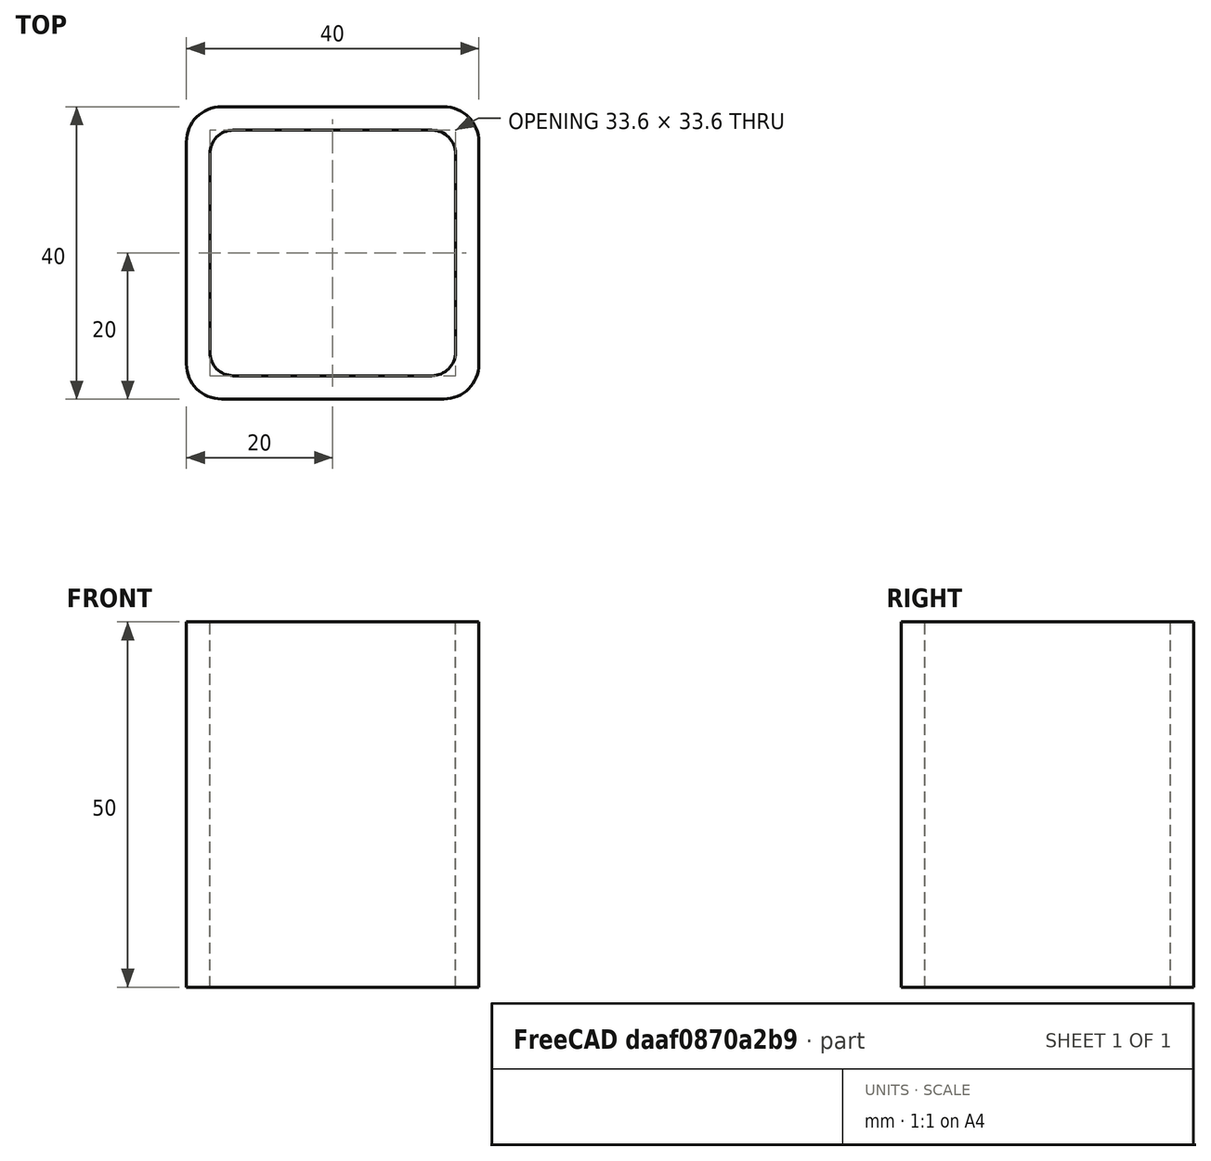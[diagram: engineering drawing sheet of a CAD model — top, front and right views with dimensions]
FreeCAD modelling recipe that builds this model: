
FCSTD DOCUMENT  (FreeCAD 0.15R4671 (Git))
Label: Square hollow section 40x40x3.2 EN10219 S235JRH
License: All rights reserved
LicenseURL: http://en.wikipedia.org/wiki/All_rights_reserved
objects: Sketcher::SketchObject×1, Part::Extrusion×1
note: 2 computed .brp shape members not serialized (recipe doc carries the construction recipe); baked Part::Feature solids carry a one-line shape summary decoded from their .brp

FEATURE [Sketcher::SketchObject] Sketch
  sketch-geometry (16):
    g0: LineSegment StartX=-13.6 StartY=16.8 StartZ=0 EndX=13.6 EndY=16.8 EndZ=0
    g1: LineSegment StartX=16.8 StartY=13.6 StartZ=0 EndX=16.8 EndY=-13.6 EndZ=0
    g2: LineSegment StartX=13.6 StartY=-16.8 StartZ=0 EndX=-13.6 EndY=-16.8 EndZ=0
    g3: LineSegment StartX=-16.8 StartY=-13.6 StartZ=0 EndX=-16.8 EndY=13.6 EndZ=0
    g4: LineSegment StartX=-15.2 StartY=20 StartZ=0 EndX=15.2 EndY=20 EndZ=0
    g5: LineSegment StartX=20 StartY=15.2 StartZ=0 EndX=20 EndY=-15.2 EndZ=0
    g6: LineSegment StartX=15.2 StartY=-20 StartZ=0 EndX=-15.2 EndY=-20 EndZ=0
    g7: LineSegment StartX=-20 StartY=-15.2 StartZ=0 EndX=-20 EndY=15.2 EndZ=0
    g8: ArcOfCircle CenterX=-13.6 CenterY=13.6 CenterZ=0 NormalX=0 NormalY=0 NormalZ=1 Radius=3.2 StartAngle=1.5708 EndAngle=3.14159
    g9: ArcOfCircle CenterX=13.6 CenterY=13.6 CenterZ=0 NormalX=0 NormalY=0 NormalZ=1 Radius=3.2 StartAngle=0 EndAngle=1.5708
    g10: ArcOfCircle CenterX=13.6 CenterY=-13.6 CenterZ=0 NormalX=0 NormalY=0 NormalZ=1 Radius=3.2 StartAngle=4.71239 EndAngle=6.28319
    g11: ArcOfCircle CenterX=-13.6 CenterY=-13.6 CenterZ=0 NormalX=0 NormalY=0 NormalZ=1 Radius=3.2 StartAngle=3.14159 EndAngle=4.71239
    g12: ArcOfCircle CenterX=15.2 CenterY=15.2 CenterZ=0 NormalX=0 NormalY=0 NormalZ=1 Radius=4.8 StartAngle=0 EndAngle=1.5708
    g13: ArcOfCircle CenterX=15.2 CenterY=-15.2 CenterZ=0 NormalX=0 NormalY=0 NormalZ=1 Radius=4.8 StartAngle=4.71239 EndAngle=6.28319
    g14: ArcOfCircle CenterX=-15.2 CenterY=-15.2 CenterZ=0 NormalX=0 NormalY=0 NormalZ=1 Radius=4.8 StartAngle=3.14159 EndAngle=4.71239
    g15: ArcOfCircle CenterX=-15.2 CenterY=15.2 CenterZ=0 NormalX=0 NormalY=0 NormalZ=1 Radius=4.8 StartAngle=1.5708 EndAngle=3.14159
  constraints (36):
    c: Horizontal(g2)
    c: Vertical(g3)
    c: Horizontal(g6)
    c: Vertical(g7)
    c: Tangent(g3,g8) = 1.5708
    c: Tangent(g0,g8) = 1.5708
    c: Tangent(g0,g9) = 1.5708
    c: Tangent(g1,g9) = 1.5708
    c: Tangent(g1,g10) = 1.5708
    c: Tangent(g2,g10) = 1.5708
    c: Tangent(g2,g11) = 1.5708
    c: Tangent(g3,g11) = 1.5708
    c: Tangent(g4,g12) = 1.5708
    c: Tangent(g5,g12) = 1.5708
    c: Tangent(g5,g13) = 1.5708
    c: Tangent(g6,g13) = 1.5708
    c: Tangent(g6,g14) = 1.5708
    c: Tangent(g7,g14) = 1.5708
    c: Tangent(g7,g15) = 1.5708
    c: Tangent(g4,g15) = 1.5708
    c: Equal(g9,g8)
    c: Equal(g9,g11)
    c: Equal(g9,g10)
    c: Equal(g12,g15)
    c: Equal(g12,g14)
    c: Equal(g12,g13)
    c: Symmetric(g4,g6,g-1)
    c: Symmetric(g7,g5,g-2)
    c: DistanceY(g4,g6) = -40
    c: DistanceX(g7,g5) = 40
    c: Symmetric(g3,g1,g-2)
    c: Symmetric(g0,g2,g-1)
    c: DistanceY(g0,g4) = 3.2
    c: DistanceX(g5,g1) = -3.2
    c: Radius(g9) = 3.2
    c: Radius(g12) = 4.8
FEATURE [Part::Extrusion] Extrude  label="Square hollow section 40x40x3.2 EN10219 S235JRH"
  Base = -> Sketch
  Dir = (0,0,50)
  Solid = true
